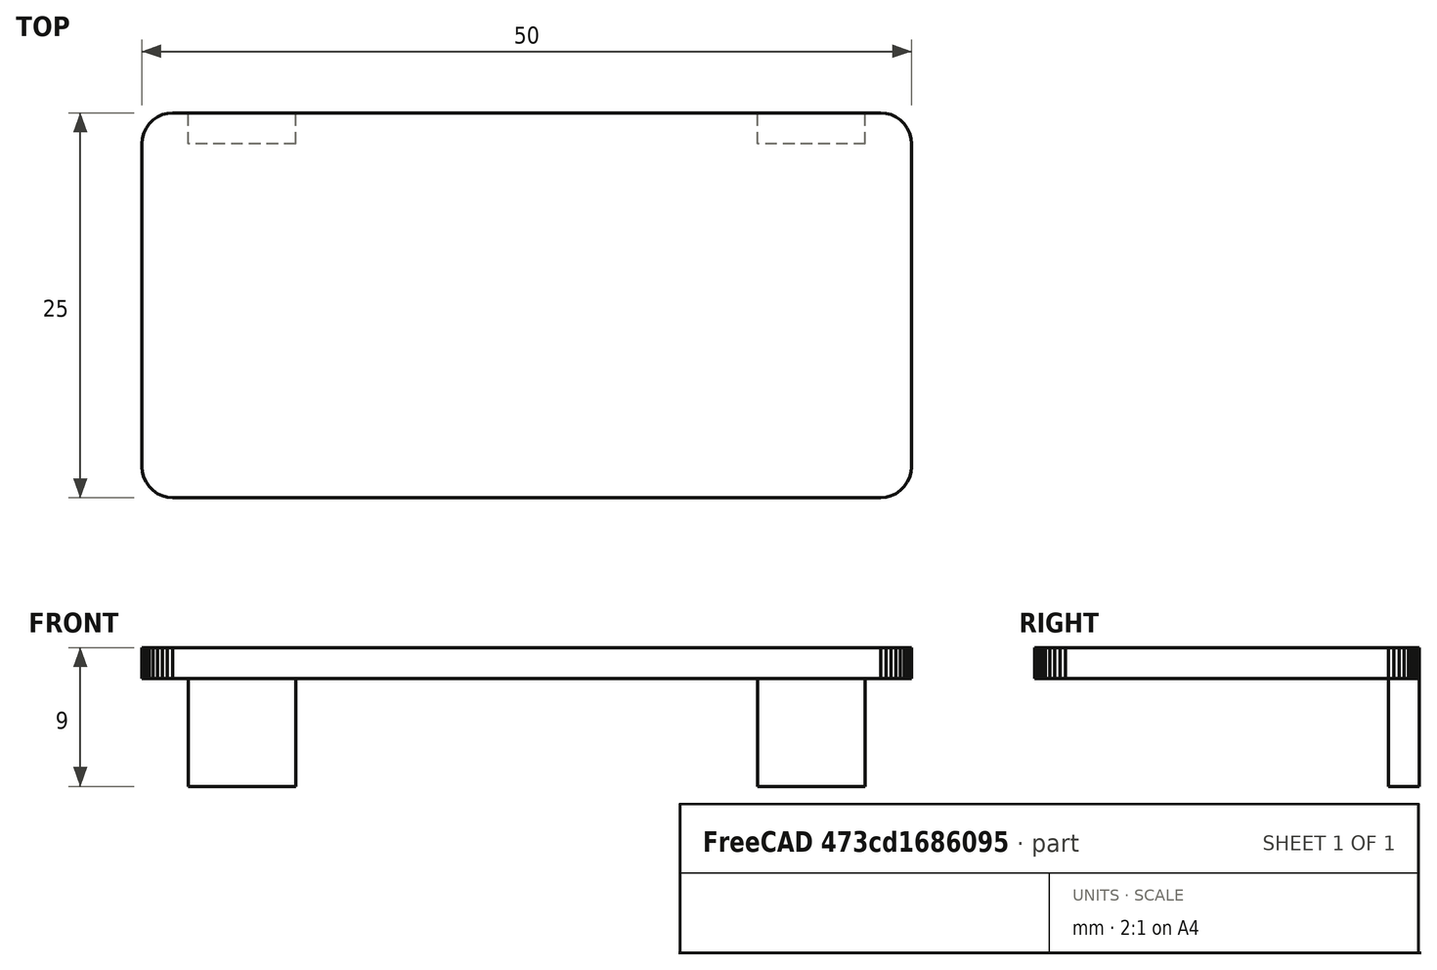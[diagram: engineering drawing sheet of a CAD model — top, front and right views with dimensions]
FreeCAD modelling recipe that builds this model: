
FCSTD DOCUMENT  (FreeCAD 0.16R6706 (Git))
Label: base mas carcasa
License: All rights reserved
LicenseURL: http://en.wikipedia.org/wiki/All_rights_reserved
objects: Part::Box×2, Part::MultiFuse×2, Part::Feature×1
note: 5 computed .brp shape members not serialized (recipe doc carries the construction recipe); baked Part::Feature solids carry a one-line shape summary decoded from their .brp

FEATURE [Part::Feature] ultrasonic_lid001001_solid  label="ultrasonic_lid002 (Solid)"
  Placement = pos=(0,0,-12) rot=(0,0,1;0rad)
  shape: bbox 50 x 25 x 2 mm, 42 faces (baked)
FEATURE [Part::Box] Box  label="Cubo"
  Height = 9
  Length = 7
  Placement = pos=(1,-2,-19) rot=(0,0,1;0rad)
  Width = 2
FEATURE [Part::Box] Box001  label="Cubo001"
  Height = 9
  Length = 7
  Placement = pos=(38,-2,-19) rot=(0,0,1;0rad)
  Width = 2
FEATURE [Part::MultiFuse] Fusion
  Shapes = -> [Box,Box001]
FEATURE [Part::MultiFuse] Fusion001  label="base del sonar"
  Placement = pos=(46,21,0) rot=(0,0,1;3.14159rad)
  Shapes = -> [ultrasonic_lid001001_solid,Fusion]
